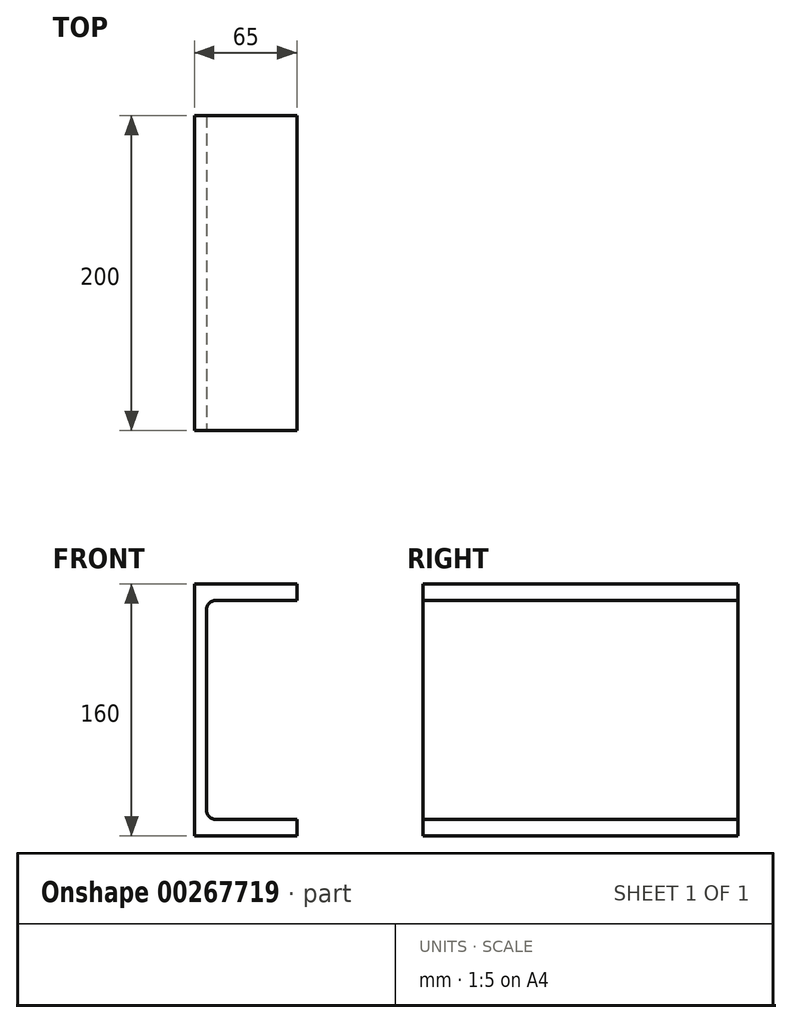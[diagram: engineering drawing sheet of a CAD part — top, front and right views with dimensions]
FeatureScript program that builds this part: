
annotation { "Feature Type Name" : "Feature", "Feature Type Description" : "" }
export const myFeature = defineFeature(function(context is Context, id is Id, definition is map)
    precondition{}
    {
        {
            var Q0;
            Q0=qCreatedBy(makeId("Front.planeOp"),FACE);
            var sketch = newSketch(context, id + "F0", { "sketchPlane" : qUnion([Q0])});
            skLineSegment(sketch, "E0.bottom", {"start": v(32.5, 80) * mm, "end": v(-32.5, 80) * mm});
            skLineSegment(sketch, "E0.top", {"start": v(32.5, -80) * mm, "end": v(-32.5, -80) * mm});
            skLineSegment(sketch, "E0.left", {"start": v(32.5, 80) * mm, "end": v(32.5, 69.5) * mm});
            skLineSegment(sketch, "E0.right", {"start": v(-32.5, 80) * mm, "end": v(-32.5, -80) * mm});
            skPoint(sketch, "E0.middle", {"position": v(0, 0) * mm});
            skLineSegment(sketch, "E1.0", {"start": v(32.5, 69.5) * mm, "end": v(-19, 69.5) * mm});
            skLineSegment(sketch, "E2.0", {"start": v(32.5, -69.5) * mm, "end": v(-19, -69.5) * mm});
            skLineSegment(sketch, "E3.0", {"start": v(-25, 63.5) * mm, "end": v(-25, -63.5) * mm});
            skArc(sketch, "E4.filletArc", {"start": v(-19, 69.5) * mm, "mid": v(-23.24, 67.74) * mm, "end": v(-25, 63.5) * mm});
            skArc(sketch, "E5.filletArc", {"start": v(-25, -63.5) * mm, "mid": v(-23.24, -67.74) * mm, "end": v(-19, -69.5) * mm});
            skLineSegment(sketch, "E6.trimOffspring", {"start": v(32.5, -69.5) * mm, "end": v(32.5, -80) * mm});
            skSolve(sketch);
        }
        {
            var Q0;
            {var subQ3=sQuery(id+"F0.wireOp",EDGE,"E0.bottom");Q0=makeQuery(id+"F0.imprint","IMPRINT",FACE,{"disambiguationData":[TD([[makeQuery(id+"F0.imprint","IMPRINT",EDGE,{"derivedFrom":subQ3}),1.0]])]});}
            extrude(context, id + "F1", {"entities" : qUnion([Q0]), "oppositeDirection" : true, "depth" : 200 * mm});
        }
    });
